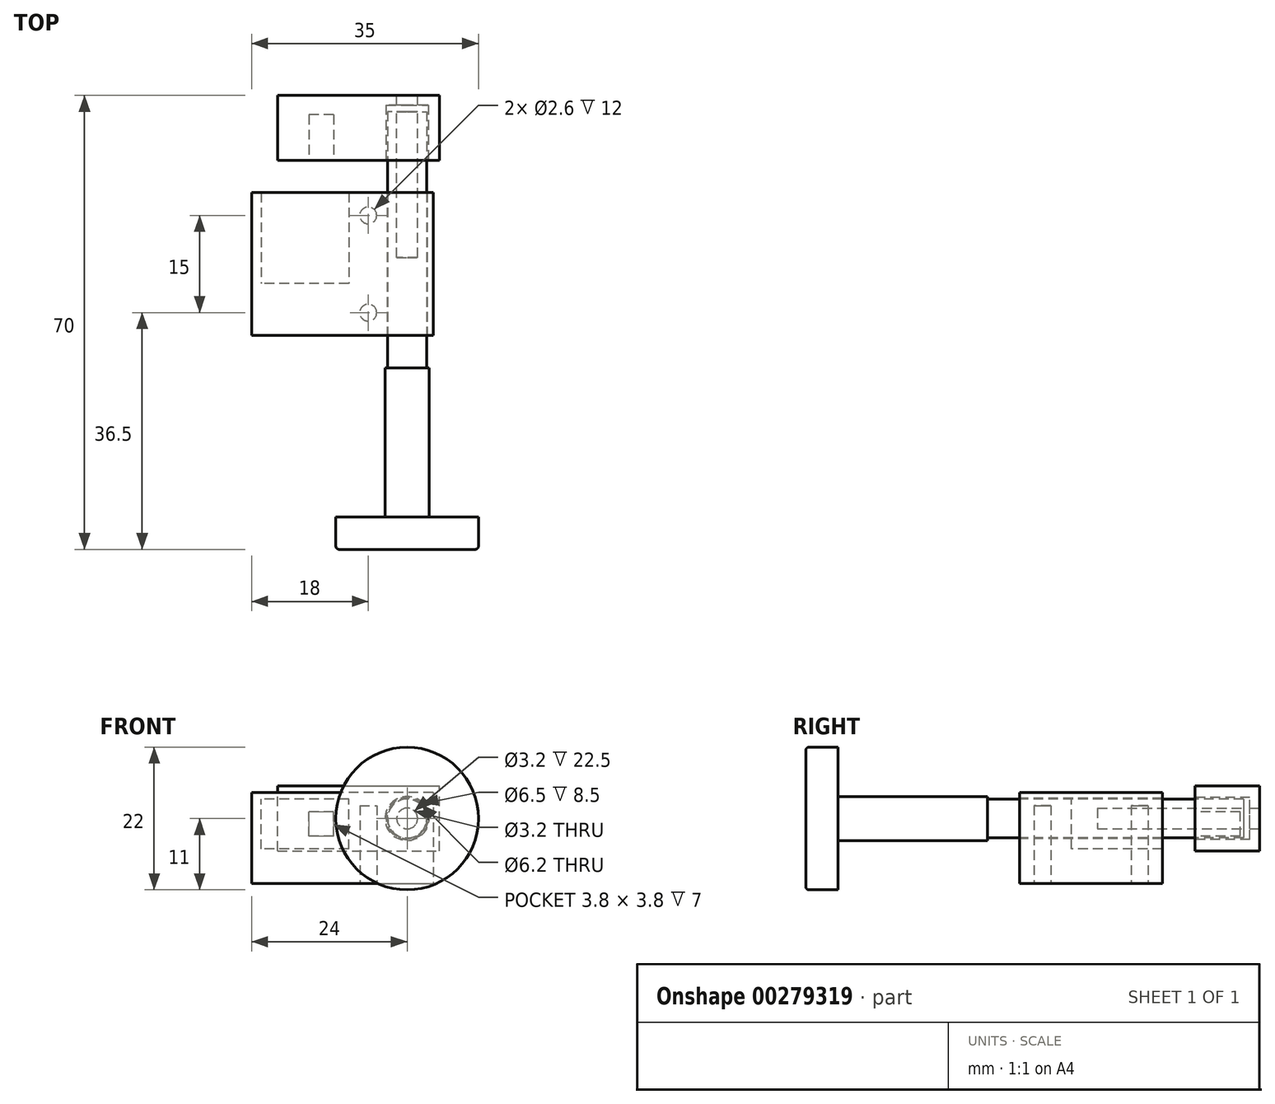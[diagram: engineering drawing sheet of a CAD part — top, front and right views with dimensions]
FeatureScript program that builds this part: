
annotation { "Feature Type Name" : "Feature", "Feature Type Description" : "" }
export const myFeature = defineFeature(function(context is Context, id is Id, definition is map)
    precondition{}
    {
        {
            var Q0;
            Q0=qCreatedBy(makeId("Front.planeOp"),FACE);
            var sketch = newSketch(context, id + "F0", { "sketchPlane" : qUnion([Q0])});
            skLineSegment(sketch, "E0.bottom", {"start": v(-22, -4.85) * mm, "end": v(-50, -4.85) * mm});
            skLineSegment(sketch, "E0.top", {"start": v(-22, 4.85) * mm, "end": v(-50, 4.85) * mm});
            skLineSegment(sketch, "E0.left", {"start": v(-22, -4.85) * mm, "end": v(-22, 4.85) * mm});
            skLineSegment(sketch, "E0.right", {"start": v(-50, -4.85) * mm, "end": v(-50, 4.85) * mm});
            skPoint(sketch, "E0.middle", {"position": v(-36, 0) * mm});
            skLineSegment(sketch, "E1.bottom", {"start": v(-35, -3.85) * mm, "end": v(-48.5, -3.85) * mm});
            skLineSegment(sketch, "E1.top", {"start": v(-35, 3.85) * mm, "end": v(-48.5, 3.85) * mm});
            skLineSegment(sketch, "E1.left", {"start": v(-35, -3.85) * mm, "end": v(-35, 3.85) * mm});
            skLineSegment(sketch, "E1.right", {"start": v(-48.5, -3.85) * mm, "end": v(-48.5, 3.85) * mm});
            skPoint(sketch, "E1.middle", {"position": v(-41.75, 0) * mm});
            skLineSegment(sketch, "E2.bottom", {"start": v(-50, -4.85) * mm, "end": v(-22, -4.85) * mm});
            skLineSegment(sketch, "E2.top", {"start": v(-50, -9.15) * mm, "end": v(-22, -9.15) * mm});
            skLineSegment(sketch, "E2.left", {"start": v(-50, -4.85) * mm, "end": v(-50, -9.15) * mm});
            skLineSegment(sketch, "E2.right", {"start": v(-22, -4.85) * mm, "end": v(-22, -9.15) * mm});
            skCircle(sketch, "E3", {"center": v(-26, 0.85) * mm, "radius": 3.1 * mm});
            skSolve(sketch);
        }
        {
            var Q0;
            Q0 = qSketchRegion(id + "F0", true);
            extrude(context, id + "F1", {"entities" : qUnion([Q0]), "oppositeDirection" : true, "depth" : 22 * mm});
        }
        {
            var Q0;
            Q0=makeQuery(id+"F1.opExtrude","CAP_FACE",FACE,{"disambiguationData":[OSD([sQuery(id+"F0.wireOp",EDGE,"E0.bottom"),sQuery(id+"F0.wireOp",EDGE,"E0.top"),sQuery(id+"F0.wireOp",EDGE,"E0.left"),sQuery(id+"F0.wireOp",EDGE,"E0.right"),sQuery(id+"F0.wireOp",EDGE,"E1.bottom"),sQuery(id+"F0.wireOp",EDGE,"E1.top"),sQuery(id+"F0.wireOp",EDGE,"E1.left"),sQuery(id+"F0.wireOp",EDGE,"E1.right"),sQuery(id+"F0.wireOp",EDGE,"IlVQ0T6Q-kpas-WKJO-rE1o-QIE4vgIgB8Sl")])],"isStart":true});
            var sketch = newSketch(context, id + "F2", { "sketchPlane" : qUnion([Q0])});
            skLineSegment(sketch, "E4.bottom", {"start": v(-48.5, 3.85) * mm, "end": v(-35, 3.85) * mm});
            skLineSegment(sketch, "E4.top", {"start": v(-48.5, -3.85) * mm, "end": v(-35, -3.85) * mm});
            skLineSegment(sketch, "E4.left", {"start": v(-35, 3.85) * mm, "end": v(-35, -3.85) * mm});
            skLineSegment(sketch, "E4.right", {"start": v(-48.5, 3.85) * mm, "end": v(-48.5, -3.85) * mm});
            skSolve(sketch);
        }
        {
            var Q0;
            Q0 = qSketchRegion(id + "F2", true);
            extrude(context, id + "F3", {"entities" : qUnion([Q0]), "operationType" : NewBodyOperationType.ADD, "oppositeDirection" : true, "depth" : 8 * mm});
        }
        {
            var Q0;
            Q0=makeQuery(id+"F1.opExtrude","SWEPT_FACE",FACE,{"disambiguationData":[OSD([sQuery(id+"F0.wireOp",EDGE,"E2.top")])]});
            var sketch = newSketch(context, id + "F4", { "sketchPlane" : qUnion([Q0])});
            skCircle(sketch, "E5", {"center": v(-32, -3.5) * mm, "radius": 1.3 * mm});
            skCircle(sketch, "E6", {"center": v(-32, -18.5) * mm, "radius": 1.3 * mm});
            skSolve(sketch);
        }
        {
            var Q0;
            Q0 = qSketchRegion(id + "F4", true);
            extrude(context, id + "F5", {"entities" : qUnion([Q0]), "operationType" : NewBodyOperationType.REMOVE, "oppositeDirection" : true, "depth" : 12 * mm});
        }
        {
            var Q0;
            Q0=makeQuery(id+"F1.opExtrude","CAP_FACE",FACE,{"disambiguationData":[OSD([sQuery(id+"F0.wireOp",EDGE,"E0.top"),sQuery(id+"F0.wireOp",EDGE,"E0.left"),sQuery(id+"F0.wireOp",EDGE,"E0.right"),sQuery(id+"F0.wireOp",EDGE,"E1.bottom"),sQuery(id+"F0.wireOp",EDGE,"E1.top"),sQuery(id+"F0.wireOp",EDGE,"E1.left"),sQuery(id+"F0.wireOp",EDGE,"E1.right"),sQuery(id+"F0.wireOp",EDGE,"E2.top"),sQuery(id+"F0.wireOp",EDGE,"E2.left"),sQuery(id+"F0.wireOp",EDGE,"E2.right"),sQuery(id+"F0.wireOp",EDGE,"E3")])],"isStart":false});
            cPlane(context, id + "F6", {"entities" : qUnion([Q0]), "cplaneType" : CPlaneType.OFFSET, "offset" : 5 * mm, "width" : 150 * mm, "height" : 150 * mm});
        }
        {
            var Q0;
            Q0=qCreatedBy(makeId("Front.planeOp"),FACE);
            cPlane(context, id + "F7", {"entities" : qUnion([Q0]), "cplaneType" : CPlaneType.OFFSET, "offset" : 28 * mm, "width" : 150 * mm, "height" : 150 * mm});
        }
        {
            var Q0;
            Q0=qCreatedBy(id+"F7.planeOp",FACE);
            var sketch = newSketch(context, id + "F8", { "sketchPlane" : qUnion([Q0])});
            skCircle(sketch, "E7", {"center": v(-26, 0.85) * mm, "radius": 11 * mm});
            skSolve(sketch);
        }
        {
            var Q0;
            Q0 = qSketchRegion(id + "F8", true);
            extrude(context, id + "F9", {"entities" : qUnion([Q0]), "depth" : 5 * mm});
        }
        {
            var Q0;
            Q0=makeQuery(id+"F9.opExtrude","CAP_FACE",FACE,{"disambiguationData":[OSD([sQuery(id+"F8.wireOp",EDGE,"E7")])],"isStart":true});
            var sketch = newSketch(context, id + "F10", { "sketchPlane" : qUnion([Q0])});
            skCircle(sketch, "E8", {"center": v(26, 0.85) * mm, "radius": 3 * mm});
            skSolve(sketch);
        }
        {
            var Q0;
            Q0 = qSketchRegion(id + "F10", true);
            extrude(context, id + "F11", {"entities" : qUnion([Q0]), "operationType" : NewBodyOperationType.ADD, "depth" : 55 * mm});
        }
        {
            var Q0;
            Q0=qCreatedBy(id+"F6.planeOp",FACE);
            var sketch = newSketch(context, id + "F12", { "sketchPlane" : qUnion([Q0])});
            skLineSegment(sketch, "E9.bottom", {"start": v(46, -4.15) * mm, "end": v(21, -4.15) * mm});
            skLineSegment(sketch, "E9.top", {"start": v(46, 5.85) * mm, "end": v(21, 5.85) * mm});
            skLineSegment(sketch, "E9.left", {"start": v(46, -4.15) * mm, "end": v(46, 5.85) * mm});
            skLineSegment(sketch, "E9.right", {"start": v(21, -4.15) * mm, "end": v(21, 5.85) * mm});
            skSolve(sketch);
        }
        {
            var Q0;
            Q0 = qSketchRegion(id + "F12", true);
            extrude(context, id + "F13", {"entities" : qUnion([Q0]), "depth" : 10 * mm});
        }
        {
            var Q0;
            Q0=makeQuery(id+"F13.opExtrude","CAP_FACE",FACE,{"disambiguationData":[OSD([sQuery(id+"F12.wireOp",EDGE,"E9.bottom"),sQuery(id+"F12.wireOp",EDGE,"E9.top"),sQuery(id+"F12.wireOp",EDGE,"E9.left"),sQuery(id+"F12.wireOp",EDGE,"E9.right")])],"isStart":true});
            var sketch = newSketch(context, id + "F14", { "sketchPlane" : qUnion([Q0])});
            skLineSegment(sketch, "E10.bottom", {"start": v(-37.35, -1.9) * mm, "end": v(-41.15, -1.9) * mm});
            skLineSegment(sketch, "E10.top", {"start": v(-37.35, 1.9) * mm, "end": v(-41.15, 1.9) * mm});
            skLineSegment(sketch, "E10.left", {"start": v(-37.35, -1.9) * mm, "end": v(-37.35, 1.9) * mm});
            skLineSegment(sketch, "E10.right", {"start": v(-41.15, -1.9) * mm, "end": v(-41.15, 1.9) * mm});
            skPoint(sketch, "E10.middle", {"position": v(-39.25, 0) * mm});
            skCircle(sketch, "E11", {"center": v(-26, 0.85) * mm, "radius": 3.25 * mm});
            skSolve(sketch);
        }
        {
            var Q0;
            Q0=makeQuery(id+"F14.imprint","IMPRINT",FACE,{"disambiguationData":[TD([[makeQuery(id+"F14.imprint","IMPRINT",EDGE,{"derivedFrom":sQuery(id+"F14.wireOp",EDGE,"E10.bottom")}),-1.0]])]});
            extrude(context, id + "F15", {"entities" : qUnion([Q0]), "operationType" : NewBodyOperationType.REMOVE, "oppositeDirection" : true, "depth" : 7 * mm});
        }
        {
            var Q0;
            Q0=makeQuery(id+"F14.imprint","IMPRINT",FACE,{"disambiguationData":[TD([[makeQuery(id+"F14.imprint","IMPRINT",EDGE,{"derivedFrom":sQuery(id+"F14.wireOp",EDGE,"E11")}),1.0]])]});
            extrude(context, id + "F16", {"entities" : qUnion([Q0]), "operationType" : NewBodyOperationType.REMOVE, "oppositeDirection" : true, "depth" : 8.5 * mm});
        }
        {
            var Q0;
            Q0=makeQuery(id+"F8.imprint","IMPRINT",FACE,{"disambiguationData":[TD([[makeQuery(id+"F8.imprint","IMPRINT",EDGE,{"derivedFrom":sQuery(id+"F8.wireOp",EDGE,"E7")}),1.0]])]});
            var sketch = newSketch(context, id + "F17", { "sketchPlane" : qUnion([Q0])});
            skCircle(sketch, "E12", {"center": v(-26, 0.85) * mm, "radius": 3.4 * mm});
            skSolve(sketch);
        }
        {
            var Q0;
            Q0 = qSketchRegion(id + "F17", true);
            extrude(context, id + "F18", {"entities" : qUnion([Q0]), "operationType" : NewBodyOperationType.ADD, "oppositeDirection" : true, "depth" : 23 * mm});
        }
        {
            var Q0;
            Q0=makeQuery(id+"F11.opExtrude","CAP_FACE",FACE,{"disambiguationData":[OSD([sQuery(id+"F10.wireOp",EDGE,"E8")])],"isStart":false});
            var sketch = newSketch(context, id + "F19", { "sketchPlane" : qUnion([Q0])});
            skCircle(sketch, "E13", {"center": v(26, 0.85) * mm, "radius": 3 * mm});
            skSolve(sketch);
        }
        {
            var Q0;
            Q0 = qSketchRegion(id + "F19", true);
            extrude(context, id + "F20", {"entities" : qUnion([Q0]), "operationType" : NewBodyOperationType.ADD, "depth" : 7.5 * mm});
        }
        {
            var Q0;
            Q0=makeQuery(id+"F20.opExtrude","CAP_FACE",FACE,{"disambiguationData":[OSD([sQuery(id+"F19.wireOp",EDGE,"E13")])],"isStart":false});
            var sketch = newSketch(context, id + "F21", { "sketchPlane" : qUnion([Q0])});
            skCircle(sketch, "E14", {"center": v(26, 0.85) * mm, "radius": 1.3 * mm});
            skSolve(sketch);
        }
        {
            var Q0;
            Q0 = qSketchRegion(id + "F21", true);
            extrude(context, id + "F22", {"entities" : qUnion([Q0]), "operationType" : NewBodyOperationType.REMOVE, "oppositeDirection" : true, "depth" : 12 * mm});
        }
        {
            var Q0;
            Q0=makeQuery(id+"F13.opExtrude","CAP_FACE",FACE,{"disambiguationData":[OSD([sQuery(id+"F12.wireOp",EDGE,"E9.bottom"),sQuery(id+"F12.wireOp",EDGE,"E9.top"),sQuery(id+"F12.wireOp",EDGE,"E9.left"),sQuery(id+"F12.wireOp",EDGE,"E9.right")])],"isStart":false});
            var sketch = newSketch(context, id + "F23", { "sketchPlane" : qUnion([Q0])});
            skCircle(sketch, "E15", {"center": v(26, 0.85) * mm, "radius": 1.6 * mm});
            skSolve(sketch);
        }
        {
            var Q0;
            Q0 = qSketchRegion(id + "F23", true);
            extrude(context, id + "F24", {"entities" : qUnion([Q0]), "operationType" : NewBodyOperationType.REMOVE, "oppositeDirection" : true, "depth" : 25 * mm});
        }
        {
            var Q0;
            Q0=makeQuery(id+"F9.opExtrude","CAP_EDGE",EDGE,{"disambiguationData":[OSD([sQuery(id+"F8.wireOp",EDGE,"E7")])],"isStart":false});
            fillet(context, id + "F25", {"entities" : qUnion([Q0]), "radius" : 0.5 * mm, "tangentPropagation" : true, "allowEdgeOverflow" : false});
        }
    });
